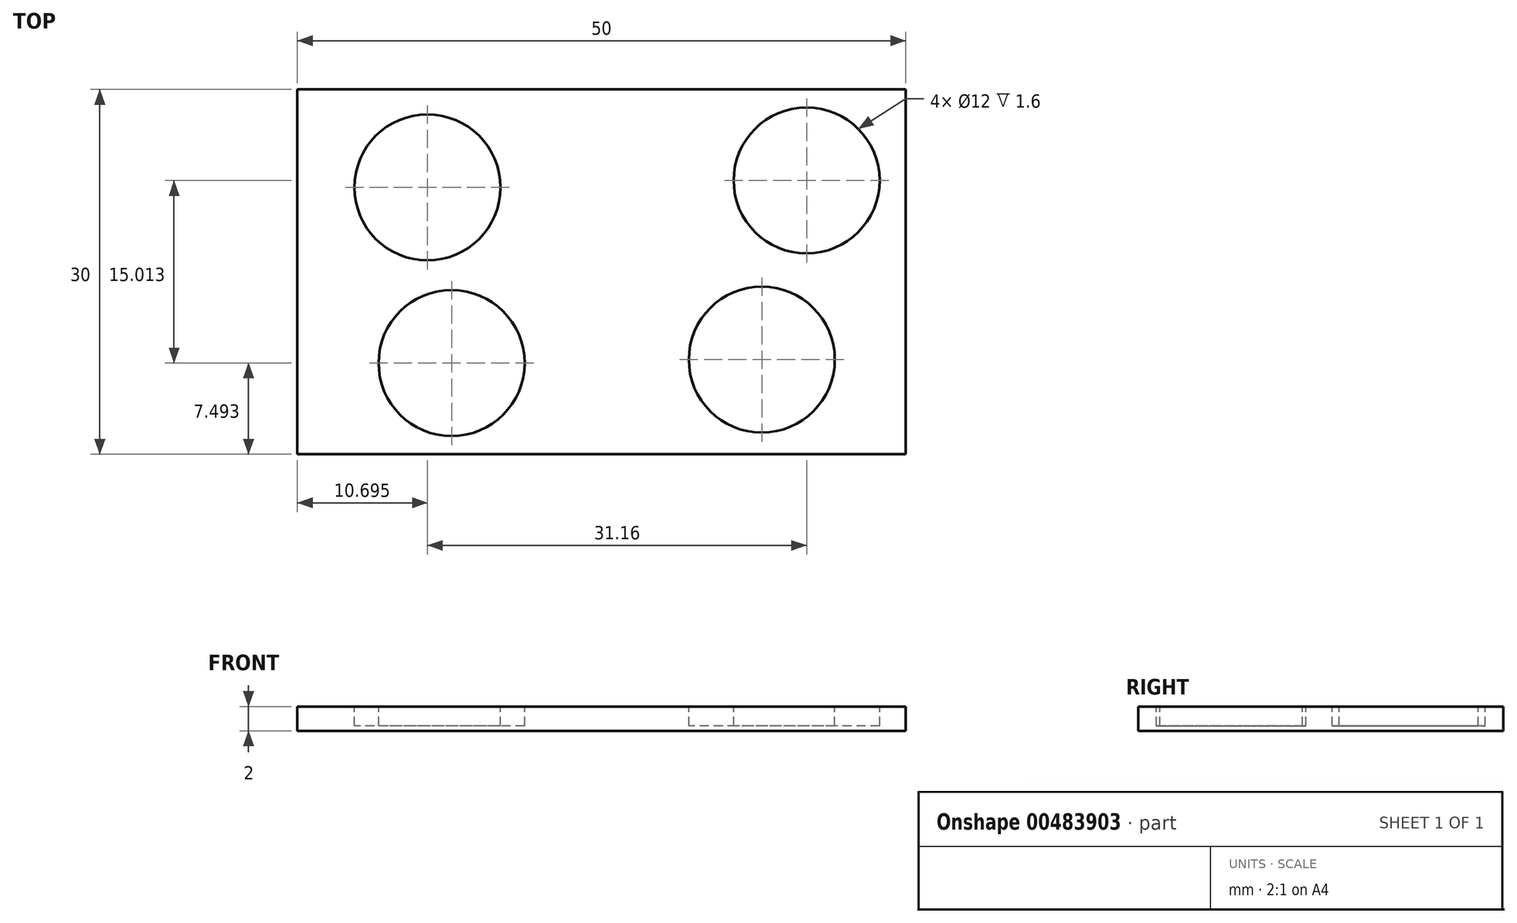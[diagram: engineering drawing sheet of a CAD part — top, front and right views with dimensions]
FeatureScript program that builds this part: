
annotation { "Feature Type Name" : "Feature", "Feature Type Description" : "" }
export const myFeature = defineFeature(function(context is Context, id is Id, definition is map)
    precondition{}
    {
        {
            var Q0;
            Q0=qCreatedBy(makeId("Top.planeOp"),FACE);
            var sketch = newSketch(context, id + "F0", { "sketchPlane" : qUnion([Q0])});
            skLineSegment(sketch, "E0.bottom", {"start": v(-25, 15) * mm, "end": v(25, 15) * mm});
            skLineSegment(sketch, "E0.top", {"start": v(-25, -15) * mm, "end": v(25, -15) * mm});
            skLineSegment(sketch, "E0.left", {"start": v(-25, 15) * mm, "end": v(-25, -15) * mm});
            skLineSegment(sketch, "E0.right", {"start": v(25, 15) * mm, "end": v(25, -15) * mm});
            skPoint(sketch, "E0.middle", {"position": v(0, 0) * mm});
            skSolve(sketch);
        }
        {
            var Q0;
            Q0=qSketchRegion(id+"F0",true);
            extrude(context, id + "F1", {"entities" : qUnion([Q0]), "oppositeDirection" : true, "depth" : 2 * mm});
        }
        {
            var Q0;
            Q0=qCreatedBy(makeId("Top.planeOp"),FACE);
            var sketch = newSketch(context, id + "F2", { "sketchPlane" : qUnion([Q0])});
            skCircle(sketch, "E1", {"center": v(-14.3, 6.94) * mm, "radius": 6 * mm});
            skCircle(sketch, "E2", {"center": v(-12.32, -7.5) * mm, "radius": 6 * mm});
            skCircle(sketch, "E3", {"center": v(13.17, -7.22) * mm, "radius": 6 * mm});
            skCircle(sketch, "E4", {"center": v(16.85, 7.5) * mm, "radius": 6 * mm});
            skSolve(sketch);
        }
        {
            var Q0;
            Q0=qSketchRegion(id+"F2",true);
            extrude(context, id + "F3", {"entities" : qUnion([Q0]), "operationType" : NewBodyOperationType.REMOVE, "oppositeDirection" : true, "offsetDistance" : 25 * mm, "depth" : 1.6 * mm});
        }
    });
